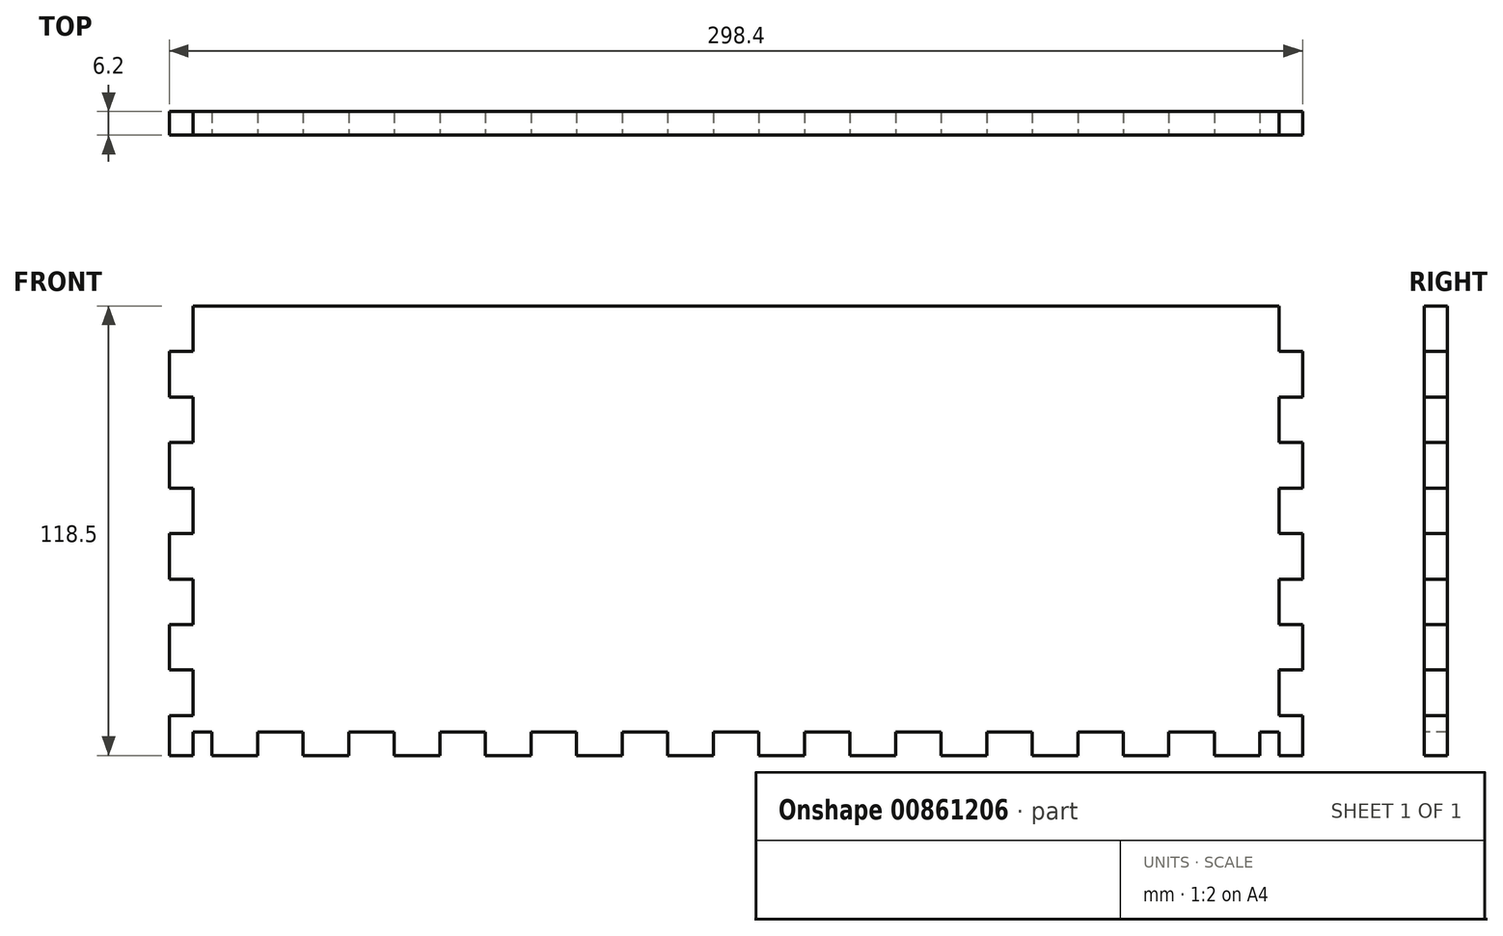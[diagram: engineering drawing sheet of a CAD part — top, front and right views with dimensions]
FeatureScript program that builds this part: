
annotation { "Feature Type Name" : "Feature", "Feature Type Description" : "" }
export const myFeature = defineFeature(function(context is Context, id is Id, definition is map)
    precondition{}
    {
        {
            var Q0;
            Q0=qCreatedBy(makeId("Front.planeOp"),FACE);
            var sketch = newSketch(context, id + "F0", { "sketchPlane" : qUnion([Q0])});
            skLineSegment(sketch, "E0.bottom", {"start": v(143, 90) * mm, "end": v(-143, 90) * mm});
            skLineSegment(sketch, "E0.top", {"start": v(143, -90) * mm, "end": v(-143, -90) * mm});
            skLineSegment(sketch, "E0.left", {"start": v(143, 90) * mm, "end": v(143, -90) * mm});
            skLineSegment(sketch, "E0.right", {"start": v(-143, 90) * mm, "end": v(-143, -90) * mm});
            skPoint(sketch, "E0.middle", {"position": v(0, 0) * mm});
            skSolve(sketch);
        }
        {
            var Q0;
            Q0=makeQuery(id+"F0.imprint","IMPRINT",FACE,{"disambiguationData":[TD([[makeQuery(id+"F0.imprint","IMPRINT",EDGE,{"derivedFrom":sQuery(id+"F0.wireOp",EDGE,"E0.bottom")}),1.0]])]});
            extrude(context, id + "F1", {"entities" : qUnion([Q0]), "depth" : 6.2 * mm, "offsetDistance" : 25 * mm});
        }
        {
            var Q0;
            Q0=makeQuery(id+"F1.opExtrude","CAP_FACE",FACE,{"disambiguationData":[OSD([sQuery(id+"F0.wireOp",EDGE,"E0.bottom"),sQuery(id+"F0.wireOp",EDGE,"E0.top"),sQuery(id+"F0.wireOp",EDGE,"E0.left"),sQuery(id+"F0.wireOp",EDGE,"E0.right")])],"isStart":false});
            var sketch = newSketch(context, id + "F2", { "sketchPlane" : qUnion([Q0])});
            skLineSegment(sketch, "E1", {"start": v(-143, -90) * mm, "end": v(-143, -28.5) * mm, "construction": true});
            skLineSegment(sketch, "E2", {"start": v(-143, -28.5) * mm, "end": v(0, -28.5) * mm, "construction": true});
            skLineSegment(sketch, "E3", {"start": v(0, -28.5) * mm, "end": v(0, -22.3) * mm, "construction": true});
            skLineSegment(sketch, "E4.bottom", {"start": v(6, -22.3) * mm, "end": v(-6, -22.3) * mm});
            skLineSegment(sketch, "E4.top", {"start": v(6, -28.5) * mm, "end": v(-6, -28.5) * mm});
            skLineSegment(sketch, "E4.left", {"start": v(6, -22.3) * mm, "end": v(6, -28.5) * mm});
            skLineSegment(sketch, "E4.right", {"start": v(-6, -22.3) * mm, "end": v(-6, -28.5) * mm});
            skPoint(sketch, "E4.middle", {"position": v(0, -25.4) * mm});
            skLineSegment(sketch, "E5.1.0.0", {"start": v(30, -22.3) * mm, "end": v(18, -22.3) * mm});
            skLineSegment(sketch, "E5.1.0.1", {"start": v(30, -22.3) * mm, "end": v(30, -28.5) * mm});
            skLineSegment(sketch, "E5.1.0.2", {"start": v(30, -28.5) * mm, "end": v(18, -28.5) * mm});
            skLineSegment(sketch, "E5.1.0.3", {"start": v(18, -22.3) * mm, "end": v(18, -28.5) * mm});
            skLineSegment(sketch, "E5.2.0.0", {"start": v(54, -22.3) * mm, "end": v(42, -22.3) * mm});
            skLineSegment(sketch, "E5.2.0.1", {"start": v(54, -22.3) * mm, "end": v(54, -28.5) * mm});
            skLineSegment(sketch, "E5.2.0.2", {"start": v(54, -28.5) * mm, "end": v(42, -28.5) * mm});
            skLineSegment(sketch, "E5.2.0.3", {"start": v(42, -22.3) * mm, "end": v(42, -28.5) * mm});
            skLineSegment(sketch, "E5.3.0.0", {"start": v(78, -22.3) * mm, "end": v(66, -22.3) * mm});
            skLineSegment(sketch, "E5.3.0.1", {"start": v(78, -22.3) * mm, "end": v(78, -28.5) * mm});
            skLineSegment(sketch, "E5.3.0.2", {"start": v(78, -28.5) * mm, "end": v(66, -28.5) * mm});
            skLineSegment(sketch, "E5.3.0.3", {"start": v(66, -22.3) * mm, "end": v(66, -28.5) * mm});
            skLineSegment(sketch, "E5.4.0.0", {"start": v(102, -22.3) * mm, "end": v(90, -22.3) * mm});
            skLineSegment(sketch, "E5.4.0.1", {"start": v(102, -22.3) * mm, "end": v(102, -28.5) * mm});
            skLineSegment(sketch, "E5.4.0.2", {"start": v(102, -28.5) * mm, "end": v(90, -28.5) * mm});
            skLineSegment(sketch, "E5.4.0.3", {"start": v(90, -22.3) * mm, "end": v(90, -28.5) * mm});
            skLineSegment(sketch, "E5.5.0.0", {"start": v(126, -22.3) * mm, "end": v(114, -22.3) * mm});
            skLineSegment(sketch, "E5.5.0.1", {"start": v(126, -22.3) * mm, "end": v(126, -28.5) * mm});
            skLineSegment(sketch, "E5.5.0.2", {"start": v(126, -28.5) * mm, "end": v(114, -28.5) * mm});
            skLineSegment(sketch, "E5.5.0.3", {"start": v(114, -22.3) * mm, "end": v(114, -28.5) * mm});
            skLineSegment(sketch, "E5.direction1", {"start": v(-6, -22.3) * mm, "end": v(18, -22.3) * mm, "construction": true});
            skLineSegment(sketch, "E6.MirrorCS", {"start": v(-78, -22.3) * mm, "end": v(-78, -28.5) * mm});
            skLineSegment(sketch, "E7.MirrorCS", {"start": v(-66, -22.3) * mm, "end": v(-66, -28.5) * mm});
            skLineSegment(sketch, "E8.MirrorCS", {"start": v(-102, -22.3) * mm, "end": v(-102, -28.5) * mm});
            skLineSegment(sketch, "E9.MirrorCS", {"start": v(-90, -22.3) * mm, "end": v(-90, -28.5) * mm});
            skLineSegment(sketch, "E10.MirrorCS", {"start": v(-54, -22.3) * mm, "end": v(-54, -28.5) * mm});
            skLineSegment(sketch, "E11.MirrorCS", {"start": v(-42, -22.3) * mm, "end": v(-42, -28.5) * mm});
            skLineSegment(sketch, "E12.MirrorCS", {"start": v(-126, -22.3) * mm, "end": v(-126, -28.5) * mm});
            skLineSegment(sketch, "E13.MirrorCS", {"start": v(-18, -22.3) * mm, "end": v(-18, -28.5) * mm});
            skLineSegment(sketch, "E14.MirrorCS", {"start": v(-30, -22.3) * mm, "end": v(-30, -28.5) * mm});
            skLineSegment(sketch, "E15.MirrorCS", {"start": v(-114, -22.3) * mm, "end": v(-114, -28.5) * mm});
            skLineSegment(sketch, "E16.MirrorCS", {"start": v(-78, -28.5) * mm, "end": v(-66, -28.5) * mm});
            skLineSegment(sketch, "E17.MirrorCS", {"start": v(-102, -22.3) * mm, "end": v(-90, -22.3) * mm});
            skLineSegment(sketch, "E18.MirrorCS", {"start": v(-102, -28.5) * mm, "end": v(-90, -28.5) * mm});
            skLineSegment(sketch, "E19.MirrorCS", {"start": v(-126, -22.3) * mm, "end": v(-114, -22.3) * mm});
            skLineSegment(sketch, "E20.MirrorCS", {"start": v(-54, -22.3) * mm, "end": v(-42, -22.3) * mm});
            skLineSegment(sketch, "E21.MirrorCS", {"start": v(-54, -28.5) * mm, "end": v(-42, -28.5) * mm});
            skLineSegment(sketch, "E22.MirrorCS", {"start": v(-78, -22.3) * mm, "end": v(-66, -22.3) * mm});
            skLineSegment(sketch, "E23.MirrorCS", {"start": v(-126, -28.5) * mm, "end": v(-114, -28.5) * mm});
            skLineSegment(sketch, "E24.MirrorCS", {"start": v(-30, -22.3) * mm, "end": v(-18, -22.3) * mm});
            skLineSegment(sketch, "E25.MirrorCS", {"start": v(-30, -28.5) * mm, "end": v(-18, -28.5) * mm});
            skLineSegment(sketch, "E26.0.6.0", {"start": v(150, -22.3) * mm, "end": v(138, -22.3) * mm});
            skLineSegment(sketch, "E26.3.6.0", {"start": v(150, -22.3) * mm, "end": v(150, -28.5) * mm});
            skLineSegment(sketch, "E26.6.6.0", {"start": v(150, -28.5) * mm, "end": v(138, -28.5) * mm});
            skLineSegment(sketch, "E26.9.6.0", {"start": v(138, -22.3) * mm, "end": v(138, -28.5) * mm});
            skLineSegment(sketch, "E27.MirrorCS", {"start": v(-150, -22.3) * mm, "end": v(-138, -22.3) * mm});
            skLineSegment(sketch, "E28.MirrorCS", {"start": v(-150, -28.5) * mm, "end": v(-138, -28.5) * mm});
            skLineSegment(sketch, "E29.MirrorCS", {"start": v(-138, -22.3) * mm, "end": v(-138, -28.5) * mm});
            skLineSegment(sketch, "E30.MirrorCS", {"start": v(-150, -22.3) * mm, "end": v(-150, -28.5) * mm});
            skSolve(sketch);
        }
        {
            var Q0;
            Q0=makeQuery(id+"F2.imprint","IMPRINT",FACE,{"disambiguationData":[TD([[makeQuery(id+"F2.imprint","IMPRINT",EDGE,{"derivedFrom":sQuery(id+"F2.wireOp",EDGE,"E12.MirrorCS")}),1.0]])]});
            var Q1;
            Q1=makeQuery(id+"F2.imprint","IMPRINT",FACE,{"disambiguationData":[TD([[makeQuery(id+"F2.imprint","IMPRINT",EDGE,{"derivedFrom":sQuery(id+"F2.wireOp",EDGE,"E8.MirrorCS")}),1.0]])]});
            var Q2;
            Q2=makeQuery(id+"F2.imprint","IMPRINT",FACE,{"disambiguationData":[TD([[makeQuery(id+"F2.imprint","IMPRINT",EDGE,{"derivedFrom":sQuery(id+"F2.wireOp",EDGE,"E6.MirrorCS")}),1.0]])]});
            var Q3;
            Q3=makeQuery(id+"F2.imprint","IMPRINT",FACE,{"disambiguationData":[TD([[makeQuery(id+"F2.imprint","IMPRINT",EDGE,{"derivedFrom":sQuery(id+"F2.wireOp",EDGE,"E10.MirrorCS")}),1.0]])]});
            var Q4;
            Q4=makeQuery(id+"F2.imprint","IMPRINT",FACE,{"disambiguationData":[TD([[makeQuery(id+"F2.imprint","IMPRINT",EDGE,{"derivedFrom":sQuery(id+"F2.wireOp",EDGE,"E13.MirrorCS")}),-1.0]])]});
            var Q5;
            Q5=makeQuery(id+"F2.imprint","IMPRINT",FACE,{"disambiguationData":[TD([[makeQuery(id+"F2.imprint","IMPRINT",EDGE,{"derivedFrom":sQuery(id+"F2.wireOp",EDGE,"E4.bottom")}),1.0]])]});
            var Q6;
            Q6=makeQuery(id+"F2.imprint","IMPRINT",FACE,{"disambiguationData":[TD([[makeQuery(id+"F2.imprint","IMPRINT",EDGE,{"derivedFrom":sQuery(id+"F2.wireOp",EDGE,"E5.1.0.0")}),1.0]])]});
            var Q7;
            Q7=makeQuery(id+"F2.imprint","IMPRINT",FACE,{"disambiguationData":[TD([[makeQuery(id+"F2.imprint","IMPRINT",EDGE,{"derivedFrom":sQuery(id+"F2.wireOp",EDGE,"E5.2.0.0")}),1.0]])]});
            var Q8;
            Q8=makeQuery(id+"F2.imprint","IMPRINT",FACE,{"disambiguationData":[TD([[makeQuery(id+"F2.imprint","IMPRINT",EDGE,{"derivedFrom":sQuery(id+"F2.wireOp",EDGE,"E5.3.0.0")}),1.0]])]});
            var Q9;
            Q9=makeQuery(id+"F2.imprint","IMPRINT",FACE,{"disambiguationData":[TD([[makeQuery(id+"F2.imprint","IMPRINT",EDGE,{"derivedFrom":sQuery(id+"F2.wireOp",EDGE,"E5.4.0.0")}),1.0]])]});
            var Q10;
            Q10=makeQuery(id+"F2.imprint","IMPRINT",FACE,{"disambiguationData":[TD([[makeQuery(id+"F2.imprint","IMPRINT",EDGE,{"derivedFrom":sQuery(id+"F2.wireOp",EDGE,"E5.5.0.0")}),1.0]])]});
            var Q11;
            {var subQ0=sQuery(id+"F2.wireOp",EDGE,"E29.MirrorCS");Q11=makeQuery(id+"F2.imprint","IMPRINT",FACE,{"disambiguationData":[TD([[makeQuery(id+"F2.imprint","IMPRINT",EDGE,{"derivedFrom":subQ0}),-1.0]])]});}
            var Q12;
            {var subQ0=sQuery(id+"F2.wireOp",EDGE,"E26.9.6.0");Q12=makeQuery(id+"F2.imprint","IMPRINT",FACE,{"disambiguationData":[TD([[makeQuery(id+"F2.imprint","IMPRINT",EDGE,{"derivedFrom":subQ0}),1.0]])]});}
            extrude(context, id + "F3", {"entities" : qUnion([Q0, Q1, Q2, Q3, Q4, Q5, Q6, Q7, Q8, Q9, Q10, Q11, Q12]), "operationType" : NewBodyOperationType.REMOVE, "endBound" : BoundingType.THROUGH_ALL, "oppositeDirection" : true, "depth" : 25 * mm, "offsetDistance" : 25 * mm});
        }
        {
            var Q0;
            Q0=makeQuery(id+"F1.opExtrude","CAP_FACE",FACE,{"disambiguationData":[OSD([sQuery(id+"F0.wireOp",EDGE,"E0.bottom"),sQuery(id+"F0.wireOp",EDGE,"E0.top"),sQuery(id+"F0.wireOp",EDGE,"E0.left"),sQuery(id+"F0.wireOp",EDGE,"E0.right")])],"isStart":false});
            var sketch = newSketch(context, id + "F4", { "sketchPlane" : qUnion([Q0])});
            skLineSegment(sketch, "E31.bottom", {"start": v(-143, -28.5) * mm, "end": v(143, -28.5) * mm});
            skLineSegment(sketch, "E31.top", {"start": v(-143, -90) * mm, "end": v(143, -90) * mm});
            skLineSegment(sketch, "E31.left", {"start": v(-143, -28.5) * mm, "end": v(-143, -90) * mm});
            skLineSegment(sketch, "E31.right", {"start": v(143, -28.5) * mm, "end": v(143, -90) * mm});
            skSolve(sketch);
        }
        {
            var Q0;
            Q0 = qSketchRegion(id + "F4", true);
            extrude(context, id + "F5", {"entities" : qUnion([Q0]), "operationType" : NewBodyOperationType.REMOVE, "endBound" : BoundingType.THROUGH_ALL, "oppositeDirection" : true, "depth" : 25 * mm, "offsetDistance" : 25 * mm});
        }
        {
            var Q0;
            Q0=makeQuery(id+"F1.opExtrude","CAP_FACE",FACE,{"disambiguationData":[OSD([sQuery(id+"F0.wireOp",EDGE,"E0.bottom"),sQuery(id+"F0.wireOp",EDGE,"E0.top"),sQuery(id+"F0.wireOp",EDGE,"E0.left"),sQuery(id+"F0.wireOp",EDGE,"E0.right")])],"isStart":false});
            var sketch = newSketch(context, id + "F6", { "sketchPlane" : qUnion([Q0])});
            skLineSegment(sketch, "E32", {"start": v(-143, 90) * mm, "end": v(-143, 78) * mm, "construction": true});
            skLineSegment(sketch, "E33.bottom", {"start": v(-143, 78) * mm, "end": v(-149.2, 78) * mm});
            skLineSegment(sketch, "E33.top", {"start": v(-143, 66) * mm, "end": v(-149.2, 66) * mm});
            skLineSegment(sketch, "E33.left", {"start": v(-143, 78) * mm, "end": v(-143, 66) * mm});
            skLineSegment(sketch, "E33.right", {"start": v(-149.2, 78) * mm, "end": v(-149.2, 66) * mm});
            skLineSegment(sketch, "E34.0.1.0", {"start": v(-149.2, 54) * mm, "end": v(-149.2, 42) * mm});
            skLineSegment(sketch, "E34.0.1.1", {"start": v(-143, 54) * mm, "end": v(-149.2, 54) * mm});
            skLineSegment(sketch, "E34.0.1.2", {"start": v(-143, 54) * mm, "end": v(-143, 42) * mm});
            skLineSegment(sketch, "E34.0.1.3", {"start": v(-143, 42) * mm, "end": v(-149.2, 42) * mm});
            skLineSegment(sketch, "E34.0.2.0", {"start": v(-149.2, 30) * mm, "end": v(-149.2, 18) * mm});
            skLineSegment(sketch, "E34.0.2.1", {"start": v(-143, 30) * mm, "end": v(-149.2, 30) * mm});
            skLineSegment(sketch, "E34.0.2.2", {"start": v(-143, 30) * mm, "end": v(-143, 18) * mm});
            skLineSegment(sketch, "E34.0.2.3", {"start": v(-143, 18) * mm, "end": v(-149.2, 18) * mm});
            skLineSegment(sketch, "E34.0.3.0", {"start": v(-149.2, 6) * mm, "end": v(-149.2, -6) * mm});
            skLineSegment(sketch, "E34.0.3.1", {"start": v(-143, 6) * mm, "end": v(-149.2, 6) * mm});
            skLineSegment(sketch, "E34.0.3.2", {"start": v(-143, 6) * mm, "end": v(-143, -6) * mm});
            skLineSegment(sketch, "E34.0.3.3", {"start": v(-143, -6) * mm, "end": v(-149.2, -6) * mm});
            skLineSegment(sketch, "E34.0.4.0", {"start": v(-149.2, -18) * mm, "end": v(-149.2, -28.5) * mm});
            skLineSegment(sketch, "E34.0.4.1", {"start": v(-143, -18) * mm, "end": v(-149.2, -18) * mm});
            skLineSegment(sketch, "E34.0.4.2", {"start": v(-143, -18) * mm, "end": v(-143, -28.5) * mm});
            skLineSegment(sketch, "E34.direction1", {"start": v(-149.2, 66) * mm, "end": v(-124.2, 66) * mm, "construction": true});
            skLineSegment(sketch, "E34.direction2", {"start": v(-149.2, 66) * mm, "end": v(-149.2, 42) * mm, "construction": true});
            skLineSegment(sketch, "E35", {"start": v(-143, -28.5) * mm, "end": v(-149.2, -28.5) * mm});
            skPoint(sketch, "E36.orphan", {"position": v(-149.2, -30) * mm});
            skLineSegment(sketch, "E37.MirrorCS", {"start": v(149.2, 54) * mm, "end": v(149.2, 42) * mm});
            skLineSegment(sketch, "E38.MirrorCS", {"start": v(143, 78) * mm, "end": v(149.2, 78) * mm});
            skLineSegment(sketch, "E39.MirrorCS", {"start": v(143, 42) * mm, "end": v(149.2, 42) * mm});
            skLineSegment(sketch, "E40.MirrorCS", {"start": v(143, 30) * mm, "end": v(149.2, 30) * mm});
            skLineSegment(sketch, "E41.MirrorCS", {"start": v(143, 78) * mm, "end": v(143, 66) * mm});
            skLineSegment(sketch, "E42.MirrorCS", {"start": v(143, 54) * mm, "end": v(149.2, 54) * mm});
            skLineSegment(sketch, "E43.MirrorCS", {"start": v(149.2, 6) * mm, "end": v(149.2, -6) * mm});
            skLineSegment(sketch, "E44.MirrorCS", {"start": v(143, 18) * mm, "end": v(149.2, 18) * mm});
            skLineSegment(sketch, "E45.MirrorCS", {"start": v(149.2, 66) * mm, "end": v(149.2, 42) * mm, "construction": true});
            skLineSegment(sketch, "E46.MirrorCS", {"start": v(143, -6) * mm, "end": v(149.2, -6) * mm});
            skLineSegment(sketch, "E47.MirrorCS", {"start": v(143, 6) * mm, "end": v(149.2, 6) * mm});
            skLineSegment(sketch, "E48.MirrorCS", {"start": v(149.2, 30) * mm, "end": v(149.2, 18) * mm});
            skLineSegment(sketch, "E49.MirrorCS", {"start": v(143, 6) * mm, "end": v(143, -6) * mm});
            skLineSegment(sketch, "E50.MirrorCS", {"start": v(149.2, 78) * mm, "end": v(149.2, 66) * mm});
            skLineSegment(sketch, "E51.MirrorCS", {"start": v(143, 54) * mm, "end": v(143, 42) * mm});
            skLineSegment(sketch, "E52.MirrorCS", {"start": v(143, 66) * mm, "end": v(149.2, 66) * mm});
            skLineSegment(sketch, "E53.MirrorCS", {"start": v(143, -18) * mm, "end": v(149.2, -18) * mm});
            skLineSegment(sketch, "E54.MirrorCS", {"start": v(143, 30) * mm, "end": v(143, 18) * mm});
            skLineSegment(sketch, "E55.MirrorCS", {"start": v(149.2, -18) * mm, "end": v(149.2, -28.5) * mm});
            skLineSegment(sketch, "E56.MirrorCS", {"start": v(143, 90) * mm, "end": v(143, 78) * mm, "construction": true});
            skLineSegment(sketch, "E57.MirrorCS", {"start": v(149.2, 66) * mm, "end": v(124.2, 66) * mm, "construction": true});
            skLineSegment(sketch, "E58.MirrorCS", {"start": v(143, -28.5) * mm, "end": v(149.2, -28.5) * mm});
            skLineSegment(sketch, "E59.MirrorCS", {"start": v(143, -18) * mm, "end": v(143, -28.5) * mm});
            skSolve(sketch);
        }
        {
            var Q0;
            Q0 = qSketchRegion(id + "F6", true);
            extrude(context, id + "F7", {"entities" : qUnion([Q0]), "operationType" : NewBodyOperationType.ADD, "oppositeDirection" : true, "depth" : 6.2 * mm, "offsetDistance" : 25 * mm});
        }
    });
